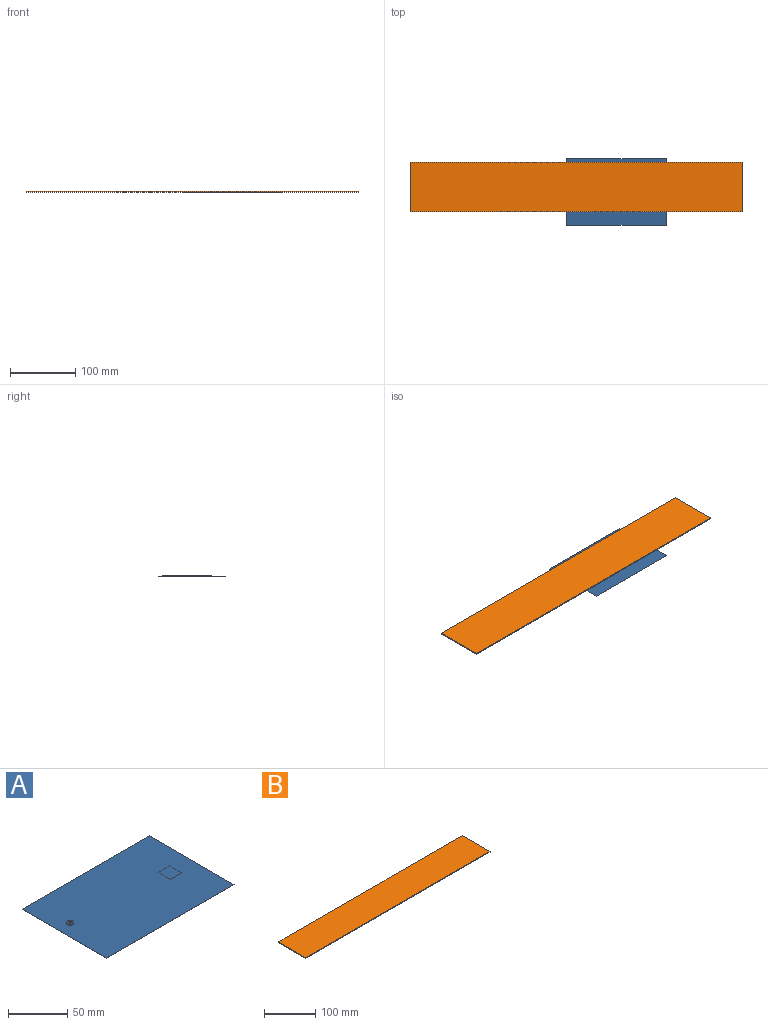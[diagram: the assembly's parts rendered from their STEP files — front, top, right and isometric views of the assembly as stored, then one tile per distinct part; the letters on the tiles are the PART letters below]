
ASSEMBLY  parts=2 mates=1
PART A: 15 faces, bbox 152.4x101.6x0.9 mm
  f0: plane 101.6x0.1mm, normal (1,0,0), area 10.3mm2, adj f1,f3,f4,f5
  f1: plane 152.4x0.1mm, normal (0,1,0), area 15.5mm2, adj f0,f2,f4,f5
  f2: plane 101.6x0.1mm, normal (-1,0,0), area 10.3mm2, adj f1,f3,f4,f5
  f3: plane 152.4x0.1mm, normal (0,-1,0), area 15.5mm2, adj f0,f2,f4,f5
  f4: plane 152.4x101.6mm, normal (0,0,1), area 15452.2mm2, adj f0,f1,f2,f3,f7
  f5: plane 152.4x101.6mm, normal (0,0,-1), area 15285.6mm2, adj f0,f1,f2,f3,f10,f11,f12,f13
  f6: cylinder r=1.13mm len=2.26mm, axis (0,0,-1), area 5.4mm2, adj f8,f9
  f7: cylinder r=3.17mm len=6.35mm, axis (0,0,-1), area 15.2mm2, adj f4,f8
  f8: plane 6.35x6.35mm, normal (0,0,1), area 27.7mm2, adj f6,f7
  f9: plane 2.26x2.26mm, normal (0,0,1), area 4mm2, adj f6
  f10: plane 13.6x0.05mm, normal (0,1,0), area 0.7mm2, adj f5,f11,f13,f14
  f11: plane 14.58x0.05mm, normal (1,0,0), area 0.7mm2, adj f5,f10,f12,f14
  f12: plane 13.6x0.05mm, normal (0,-1,0), area 0.7mm2, adj f5,f11,f13,f14
  f13: plane 14.58x0.05mm, normal (-1,0,0), area 0.7mm2, adj f5,f10,f12,f14
  f14: plane 14.58x13.6mm, normal (0,0,-1), area 198.2mm2, adj f10,f11,f12,f13
PART B: 6 faces, bbox 508x76.2x1.6 mm
  f0: plane 508x1.59mm, normal (0,-1,0), area 806.5mm2, adj f1,f3,f4,f5
  f1: plane 76.2x1.59mm, normal (1,0,0), area 121mm2, adj f0,f2,f4,f5
  f2: plane 508x1.59mm, normal (0,1,0), area 806.5mm2, adj f1,f3,f4,f5
  f3: plane 76.2x1.59mm, normal (-1,0,0), area 121mm2, adj f0,f2,f4,f5
  f4: plane 508x76.2mm, normal (0,0,1), area 38709.6mm2, adj f0,f1,f2,f3
  f5: plane 508x76.2mm, normal (0,0,-1), area 38709.6mm2, adj f0,f1,f2,f3
PLACE A t=(61.92,-7.57,-1.32)mm
PLACE B t=(0,0,-0.46)mm
MATE planar A.f6 <-> B.f5  axis (0,0,1) through (0,0,-0.46)mm
